# Revit family: Single_Hung-PGT-Aluminum-SH700d
name_source: partatom
category: Windows
revit_build: Autodesk Revit 2015 (Build: 20160512_1515(x64)
units: mm (PartAtom-declared; Revit-internal decimal feet)

## types (1)
- Refer to Type Catalog
    Analytic Construction = <None>
    Assembly Code = B2020.10
    BP Calc = 4 7/16"
    Color Glass = Glass - PGT - Clear
    Custom Design Note = The types included show default grid/size configurations.  Please reference the 'Product Style Guide' to see all standard configurations and restrictions before creating custom designs.  Please contact PGT Industries with any questions regarding custom designs.
    Default Sill Height = 36"
    Description = Aluminum Single Hung
    Finish = Metal - PGT - Paint - White
    Grid = Yes
    Grid Layout Note = To edit the grid layout ensure the 'Grid' parameter is turned on and then select an option from the 'Grid Type Bottom Sash' & 'Grid Type Top Sash' drop downs.  Please refer to the 'Product Style Guide' for standard configurations and restrictions.
    Grid Type Bottom Sash = Face_Based_Mullion_ 401 : BP9
    Grid Type Top Sash = Face_Based_Mullion_ 401 : BP9
    Height = 50"
    Height Calc Bottom = 21 7/16"
    Height Calc Top = 21 5/8"
    Manufacturer = PGT Industries
    Maximum Size = 53 1/8” x 76”
    Minimum Size = 13 1/2” x 24 3/4”.
    Model = SH700
    Product Page URL = http://www.pgtindustries.com
    Product Style Guide = http://www.pgtindustries.com
    Rough Height = 50"
    Rough Width = 30"
    Top Sash = 25"
    Type Comments = Flange, Equal Sash
    URL = http://www.pgtindustries.com
    Wall Closure = By host
    Width = 30"
    Width Calc = 26 1/2"

## geometry (parser evidence)
native form markers: Sweep x25
no freeform markers — native parametric forms only
